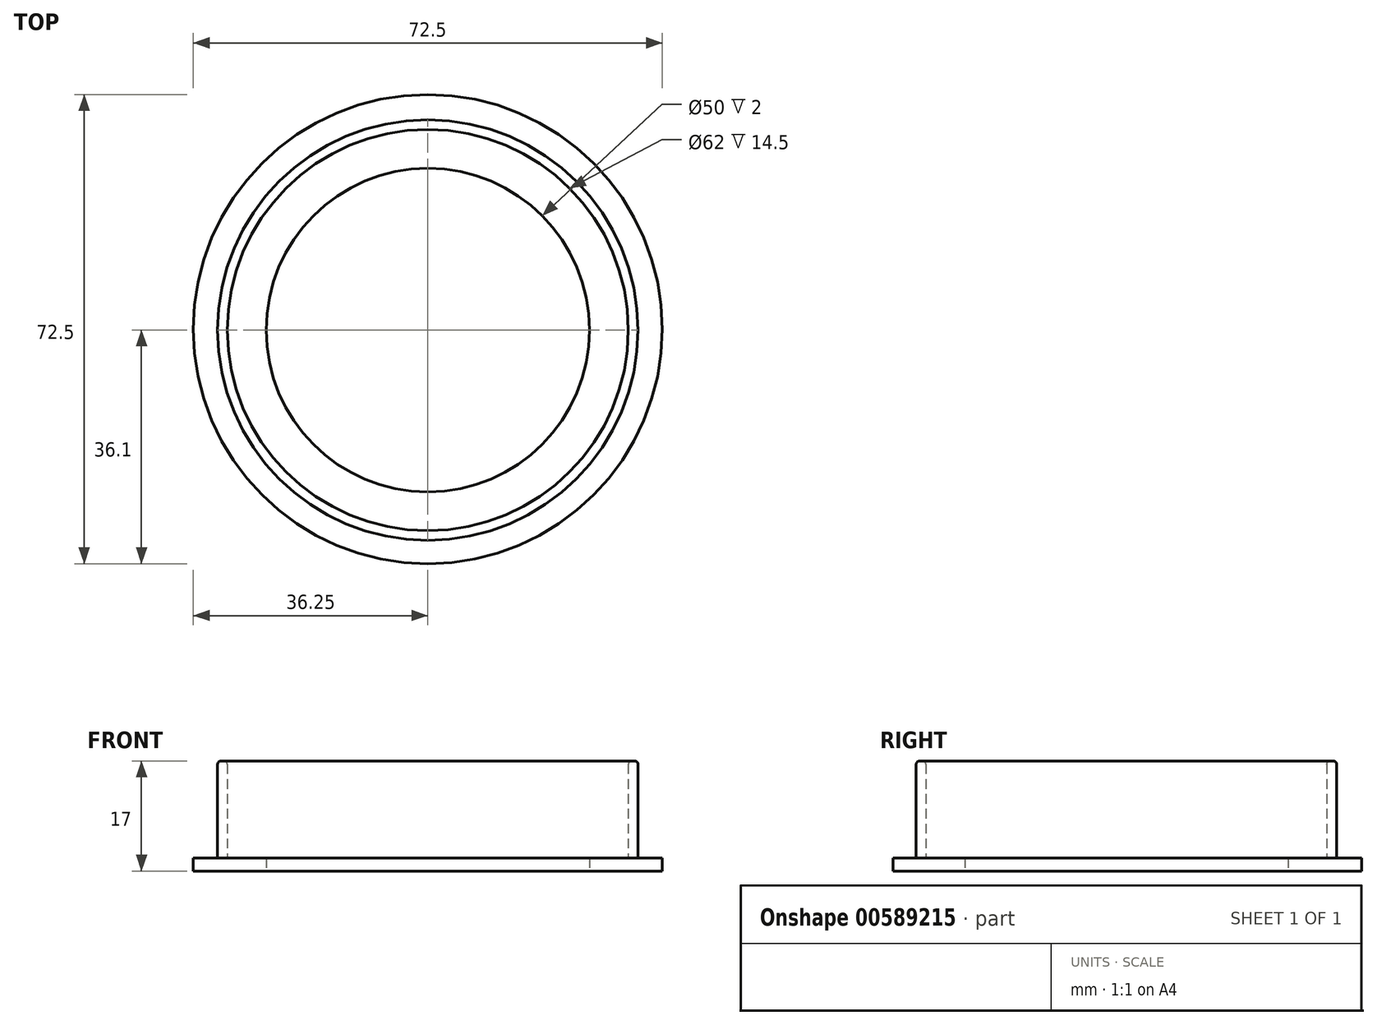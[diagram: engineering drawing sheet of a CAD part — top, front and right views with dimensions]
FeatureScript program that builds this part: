
annotation { "Feature Type Name" : "Feature", "Feature Type Description" : "" }
export const myFeature = defineFeature(function(context is Context, id is Id, definition is map)
    precondition{}
    {
        {
            var Q0;
            Q0=qCreatedBy(makeId("Top.planeOp"),FACE);
            var sketch = newSketch(context, id + "F0", { "sketchPlane" : qUnion([Q0])});
            skCircle(sketch, "E0", {"center": v(0, 0.15) * mm, "radius": 36.25 * mm});
            skCircle(sketch, "E1", {"center": v(0, 0) * mm, "radius": 25 * mm});
            skSolve(sketch);
        }
        {
            var Q0;
            Q0=qSketchRegion(id+"F0",true);
            extrude(context, id + "F1", {"entities" : qUnion([Q0]), "depth" : 2 * mm, "offsetDistance" : 25 * mm});
        }
        {
            var Q0;
            Q0=makeQuery(id+"F1.opExtrude","CAP_FACE",FACE,{"disambiguationData":[OSD([sQuery(id+"F0.wireOp",EDGE,"E0"),sQuery(id+"F0.wireOp",EDGE,"E1")])],"isStart":false});
            var sketch = newSketch(context, id + "F2", { "sketchPlane" : qUnion([Q0])});
            skArc(sketch, "E2", {"start": v(-3.49, 22.23) * mm, "mid": v(-4.23, 22.1) * mm, "end": v(-4.97, 21.94) * mm});
            skArc(sketch, "E3.trimOffspring", {"start": v(4.97, 21.94) * mm, "mid": v(4.23, 22.1) * mm, "end": v(3.49, 22.23) * mm});
            skCircle(sketch, "E4", {"center": v(0, 0) * mm, "radius": 30 * mm});
            skCircle(sketch, "E5", {"center": v(0, 0) * mm, "radius": 32.5 * mm});
            skCircle(sketch, "E6.0", {"center": v(0, 0) * mm, "radius": 31 * mm});
            skSolve(sketch);
        }
        {
            var Q0;
            Q0=qSketchRegion(id+"F2",true);
            extrude(context, id + "F3", {"entities" : qUnion([Q0]), "operationType" : NewBodyOperationType.ADD, "depth" : 15 * mm, "offsetDistance" : 25 * mm});
        }
        {
            var Q0;
            Q0=makeQuery(id+"F3.opExtrude","CAP_EDGE",EDGE,{"disambiguationData":[OSD([sQuery(id+"F2.wireOp",EDGE,"E5")])],"isStart":false});
            var Q1;
            Q1=makeQuery(id+"F3.opExtrude","CAP_EDGE",EDGE,{"disambiguationData":[OSD([sQuery(id+"F2.wireOp",EDGE,"E6.0")])],"isStart":false});
            fillet(context, id + "F4", {"entities" : qUnion([Q0, Q1]), "radius" : .5 * mm, "tangentPropagation" : true, "allowEdgeOverflow" : false});
        }
    });
